# Revit family: U_stiel US 5 20 FT
name_source: partatom
category: Generic Models
revit_build: Autodesk Revit 2017 (Build: 20190508_0315(x64)
units: mm (PartAtom-declared; Revit-internal decimal feet)

## family parameters
Always vertical = Yes
Can host rebar = No
Cut with Voids When Loaded = No
Part Type = Normal
Room Calculation Point = No
Round Connector Dimension = Use Diameter
Shared = No
Work Plane-Based = No

## types (14) — shared parameters
Cut's space = 50 mm  [stored 0.164042 ft]
Manufacturer = OBO BETTERMANN
Material = Hot dip galvanised
URL = http://www.obo-bettermann.com

## per-type parameters (varying)
| type | Cut's number | GTIN | Length | Manufacturer Art.No. |
| US 5 20 FT | 4 | 4012196959006 | 200 mm  [stored 0.656168 ft] | 6340881 |
| US 5 30 FT | 6 | 4012196959068 | 300 mm | 6340903 |
| US 5 40 FT | 8 | 4012196959129 | 400 mm  [stored 1.31234 ft] | 6340911 |
| US 5 50 FT | 10 | 4012196959181 | 500 mm  [stored 1.64042 ft] | 6340938 |
| US 5 60 FT | 12 | 4012196601752 | 600 mm | 6340946 |
| US 5 70 FT | 14 | 4012196043927 | 700 mm  [stored 2.29659 ft] | 6340950 |
| US 5 80 FT | 16 | 4012196044047 | 800 mm  [stored 2.62467 ft] | 6340954 |
| US 5 90 FT | 18 | 4012196044160 | 900 mm  [stored 2.95276 ft] | 6340958 |
| US 5 100 FT | 20 | 4012196284177 | 1000 mm  [stored 3.28084 ft] | 6340962 |
| US 5 110 FT | 22 | 4012195776277 | 1100 mm | 6340964 |
| US 5 150 FT | 30 | 4012196437597 | 1500 mm  [stored 4.92126 ft] | 6340966 |
| US 5 200 FT | 40 | 4012196437658 | 2000 mm  [stored 6.56168 ft] | 6340970 |
| US 5 300 FT | 60 | 4012196437719 | 3000 mm  [stored 9.84252 ft] | 6340989 |
| US 5 600 FT | 120 | 4012196437719 | 6000 mm  [stored 19.685 ft] | 6340997 |

note: column(s) folded — value = type name in every type: Article Type

note: [stored X ft] marks values corroborated as IEEE doubles in the binary element streams (Revit-internal decimal feet)

## geometry (parser evidence)
native form markers: Sweep x1
no freeform markers — native parametric forms only
